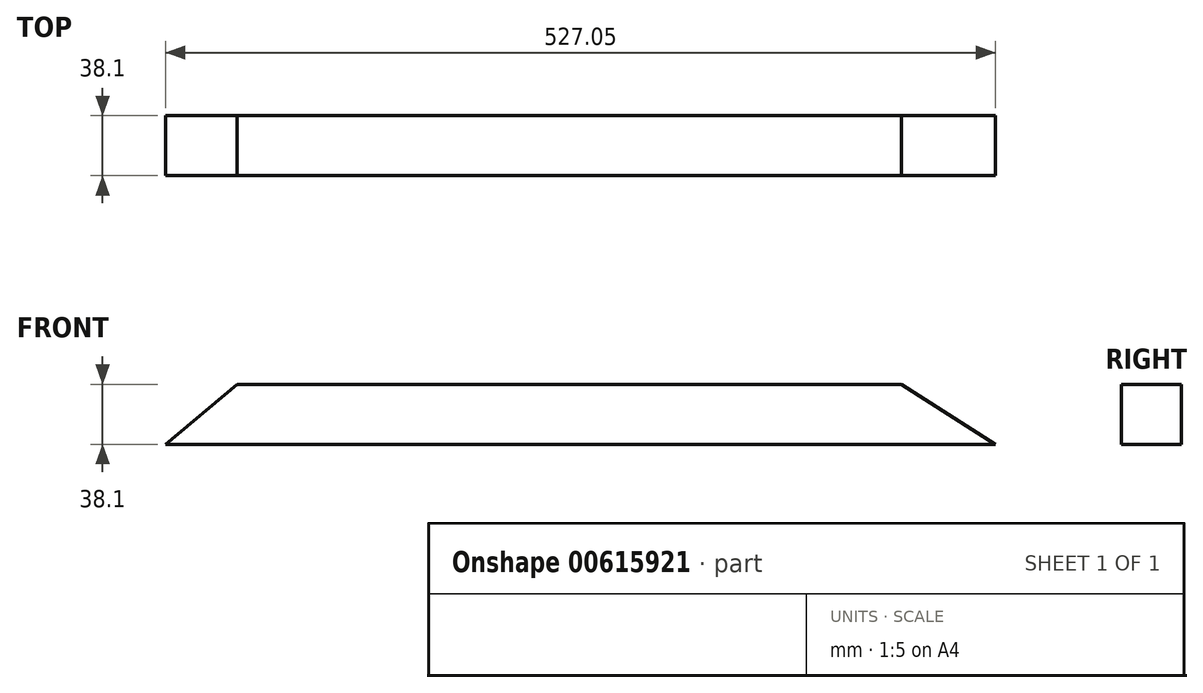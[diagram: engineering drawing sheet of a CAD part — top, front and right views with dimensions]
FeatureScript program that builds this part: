
annotation { "Feature Type Name" : "Feature", "Feature Type Description" : "" }
export const myFeature = defineFeature(function(context is Context, id is Id, definition is map)
    precondition{}
    {
        {
            var Q0;
            Q0=qCreatedBy(makeId("Front.planeOp"),FACE);
            var sketch = newSketch(context, id + "F0", { "sketchPlane" : qUnion([Q0])});
            skLineSegment(sketch, "E0.bottom", {"start": v(-538.8, 19.05) * mm, "end": v(-116.96, 19.05) * mm});
            skLineSegment(sketch, "E0.top", {"start": v(-584.2, -19.05) * mm, "end": v(-57.15, -19.05) * mm});
            skPoint(sketch, "E0.middle", {"position": v(0, 0) * mm});
            skLineSegment(sketch, "E1", {"start": v(-57.15, -19.05) * mm, "end": v(-116.96, 19.05) * mm});
            skPoint(sketch, "E0.right.start.orphan", {"position": v(584.2, 19.05) * mm});
            skLineSegment(sketch, "E2", {"start": v(-584.2, -19.05) * mm, "end": v(-538.8, 19.05) * mm});
            skPoint(sketch, "E0.left.start.orphan", {"position": v(57.15, 19.05) * mm});
            skSolve(sketch);
        }
        {
            var Q0;
            Q0 = qSketchRegion(id + "F0", true);
            extrude(context, id + "F1", {"entities" : qUnion([Q0]), "endBound" : BoundingType.SYMMETRIC, "depth" : 38.1 * mm, "offsetDistance" : 25.4 * mm});
        }
    });
